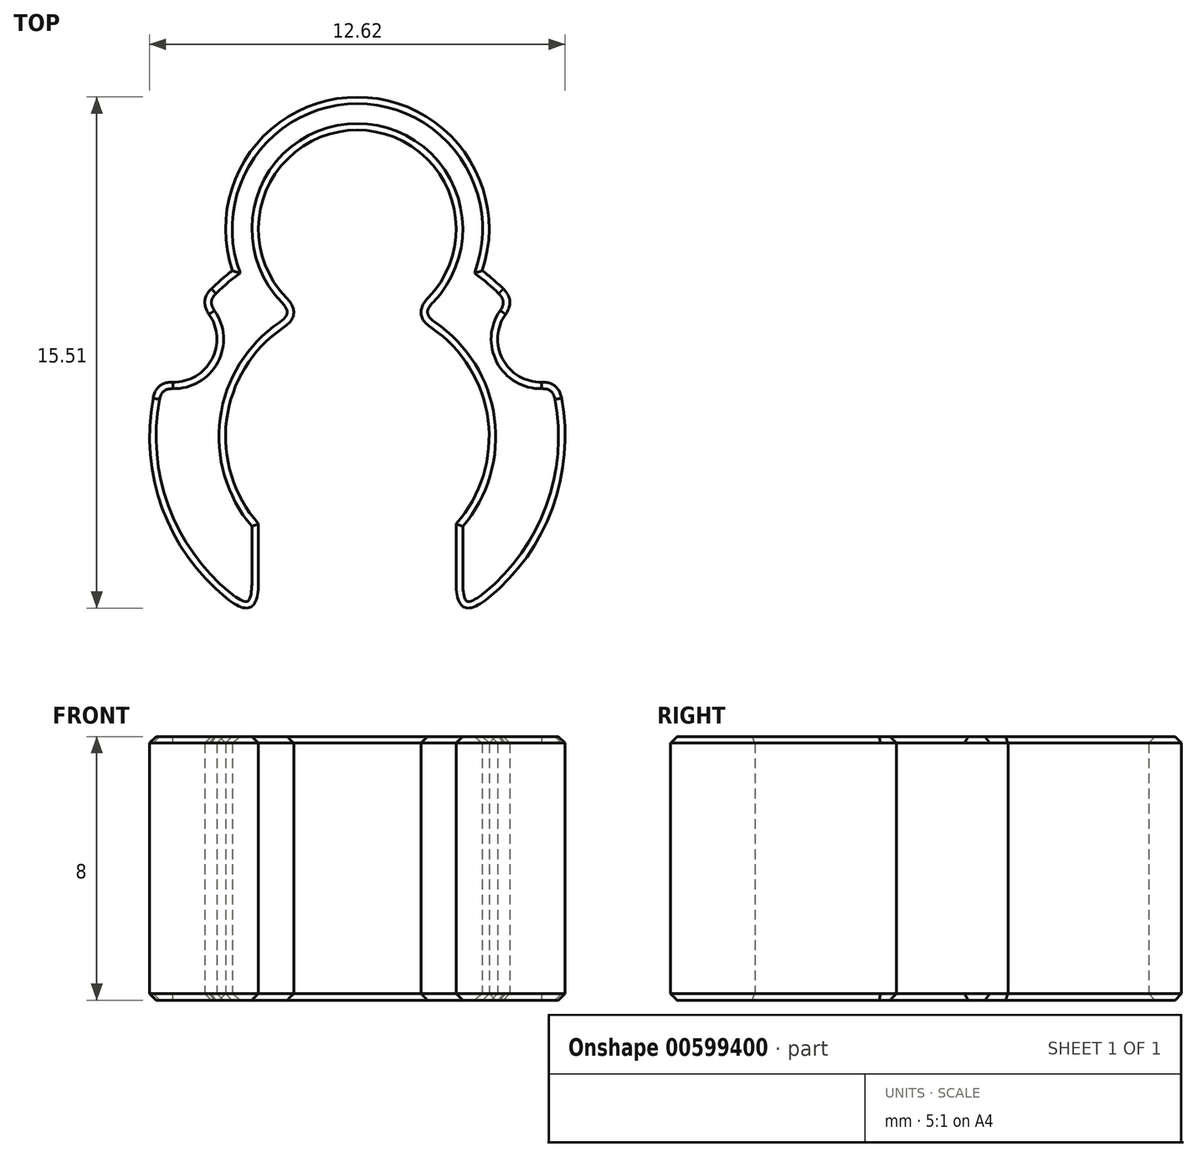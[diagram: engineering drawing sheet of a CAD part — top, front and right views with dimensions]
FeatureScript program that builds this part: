
annotation { "Feature Type Name" : "Feature", "Feature Type Description" : "" }
export const myFeature = defineFeature(function(context is Context, id is Id, definition is map)
    precondition{}
    {
        {
            var Q0;
            Q0=qCreatedBy(makeId("Top.planeOp"),FACE);
            var sketch = newSketch(context, id + "F0", { "sketchPlane" : qUnion([Q0])});
            skCircle(sketch, "E0", {"center": v(0, 0) * mm, "radius": 4 * mm});
            skCircle(sketch, "E1", {"center": v(0, 0) * mm, "radius": 6.3 * mm});
            skLineSegment(sketch, "E2.bottom", {"start": v(3, -2.65) * mm, "end": v(-3, -2.65) * mm});
            skLineSegment(sketch, "E2.top", {"start": v(3, -6.3) * mm, "end": v(-3, -6.3) * mm});
            skLineSegment(sketch, "E2.left", {"start": v(3, -2.65) * mm, "end": v(3, -6.3) * mm});
            skLineSegment(sketch, "E2.right", {"start": v(-3, -2.65) * mm, "end": v(-3, -6.3) * mm});
            skPoint(sketch, "E2.middle", {"position": v(0, -4.48) * mm});
            skCircle(sketch, "E3", {"center": v(0, 6.3) * mm, "radius": 3 * mm});
            skCircle(sketch, "E4", {"center": v(0, 6.3) * mm, "radius": 4 * mm});
            skCircle(sketch, "E5", {"center": v(-5.57, 2.96) * mm, "radius": 1.3 * mm});
            skLineSegment(sketch, "E6", {"start": v(0, 0) * mm, "end": v(-5.57, 2.96) * mm, "construction": true});
            skLineSegment(sketch, "E7", {"start": v(0, 0) * mm, "end": v(-3.8, 5.04) * mm, "construction": true});
            skLineSegment(sketch, "E8", {"start": v(0, 0) * mm, "end": v(3.8, 5.04) * mm, "construction": true});
            skLineSegment(sketch, "E9", {"start": v(0, 0) * mm, "end": v(5.57, 2.96) * mm, "construction": true});
            skCircle(sketch, "E10", {"center": v(5.57, 2.96) * mm, "radius": 1.3 * mm});
            skPoint(sketch, "E11", {"position": v(-1.5, 3.7) * mm});
            skPoint(sketch, "E12", {"position": v(1.5, 3.7) * mm});
            skSolve(sketch);
        }
        {
            var Q0;
            {var subQ3=sQuery(id+"F0.wireOp",EDGE,"E1");var subQ5=sQuery(id+"F0.wireOp",EDGE,"E4");var subQ6=makeQuery(id+"F0.imprint","INTERSECT",VERTEX,{"disambiguationData":[OD(1.0)],"derivedFrom":[subQ3,subQ5]});Q0=makeQuery(id+"F0.imprint","IMPRINT",FACE,{"disambiguationData":[TD([[makeQuery(id+"F0.imprint","IMPRINT",EDGE,{"disambiguationData":[TD([[subQ6,-1.0]])],"derivedFrom":subQ3}),1.0]])]});}
            var Q1;
            {var subQ0=sQuery(id+"F0.wireOp",EDGE,"E10");var subQ1=sQuery(id+"F0.wireOp",EDGE,"E1");var subQ9=makeQuery(id+"F0.imprint","INTERSECT",VERTEX,{"disambiguationData":[OD(0.0)],"derivedFrom":[subQ1,subQ0]});Q1=makeQuery(id+"F0.imprint","IMPRINT",FACE,{"disambiguationData":[TD([[makeQuery(id+"F0.imprint","IMPRINT",EDGE,{"disambiguationData":[TD([[subQ9,-1.0]])],"derivedFrom":subQ1}),1.0]])]});}
            var Q2;
            {var subQ0=sQuery(id+"F0.wireOp",EDGE,"E3");var subQ1=sQuery(id+"F0.wireOp",EDGE,"E0");var subQ2=makeQuery(id+"F0.imprint","INTERSECT",VERTEX,{"disambiguationData":[OD(0.0)],"derivedFrom":[subQ1,subQ0]});Q2=makeQuery(id+"F0.imprint","IMPRINT",FACE,{"disambiguationData":[TD([[makeQuery(id+"F0.imprint","IMPRINT",EDGE,{"disambiguationData":[TD([[subQ2,1.0]])],"derivedFrom":subQ1}),-1.0]])]});}
            var Q3;
            {var subQ0=sQuery(id+"F0.wireOp",EDGE,"E4");var subQ1=sQuery(id+"F0.wireOp",EDGE,"E1");var subQ2=makeQuery(id+"F0.imprint","INTERSECT",VERTEX,{"disambiguationData":[OD(0.0)],"derivedFrom":[subQ1,subQ0]});Q3=makeQuery(id+"F0.imprint","IMPRINT",FACE,{"disambiguationData":[TD([[makeQuery(id+"F0.imprint","IMPRINT",EDGE,{"disambiguationData":[TD([[subQ2,-1.0]])],"derivedFrom":subQ1}),-1.0]])]});}
            var Q4;
            {var subQ0=sQuery(id+"F0.wireOp",EDGE,"E3");var subQ1=sQuery(id+"F0.wireOp",EDGE,"E0");var subQ2=makeQuery(id+"F0.imprint","INTERSECT",VERTEX,{"disambiguationData":[OD(1.0)],"derivedFrom":[subQ1,subQ0]});Q4=makeQuery(id+"F0.imprint","IMPRINT",FACE,{"disambiguationData":[TD([[makeQuery(id+"F0.imprint","IMPRINT",EDGE,{"disambiguationData":[TD([[subQ2,-1.0]])],"derivedFrom":subQ1}),-1.0]])]});}
            extrude(context, id + "F1", {"entities" : qUnion([Q0, Q1, Q2, Q3, Q4]), "depth" : 8 * mm, "offsetDistance" : 25 * mm});
        }
        {
            var Q0;
            {var subQ0=sQuery(id+"F0.wireOp",EDGE,"E5");var subQ1=sQuery(id+"F0.wireOp",EDGE,"E1");Q0=makeQuery(id+"F1.opExtrude","SWEPT_EDGE",EDGE,{"disambiguationData":[OSD([subQ1,subQ0]),TDD([makeQuery(id+"F0.imprint","INTERSECT",VERTEX,{"disambiguationData":[OD(0.0)],"derivedFrom":[subQ1,subQ0]})])]});}
            var Q1;
            {var subQ0=sQuery(id+"F0.wireOp",EDGE,"E5");var subQ1=sQuery(id+"F0.wireOp",EDGE,"E1");Q1=makeQuery(id+"F1.opExtrude","SWEPT_EDGE",EDGE,{"disambiguationData":[OSD([subQ1,subQ0]),TDD([makeQuery(id+"F0.imprint","INTERSECT",VERTEX,{"disambiguationData":[OD(1.0)],"derivedFrom":[subQ1,subQ0]})])]});}
            var Q2;
            {var subQ0=sQuery(id+"F0.wireOp",EDGE,"E3");var subQ1=sQuery(id+"F0.wireOp",EDGE,"E0");Q2=makeQuery(id+"F1.opExtrude","SWEPT_EDGE",EDGE,{"disambiguationData":[OSD([subQ1,subQ0]),TDD([makeQuery(id+"F0.imprint","INTERSECT",VERTEX,{"disambiguationData":[OD(1.0)],"derivedFrom":[subQ1,subQ0]})])]});}
            var Q3;
            {var subQ0=sQuery(id+"F0.wireOp",EDGE,"E10");var subQ1=sQuery(id+"F0.wireOp",EDGE,"E1");Q3=makeQuery(id+"F1.opExtrude","SWEPT_EDGE",EDGE,{"disambiguationData":[OSD([subQ1,subQ0]),TDD([makeQuery(id+"F0.imprint","INTERSECT",VERTEX,{"disambiguationData":[OD(0.0)],"derivedFrom":[subQ1,subQ0]})])]});}
            var Q4;
            {var subQ0=sQuery(id+"F0.wireOp",EDGE,"E3");var subQ1=sQuery(id+"F0.wireOp",EDGE,"E0");Q4=makeQuery(id+"F1.opExtrude","SWEPT_EDGE",EDGE,{"disambiguationData":[OSD([subQ1,subQ0]),TDD([makeQuery(id+"F0.imprint","INTERSECT",VERTEX,{"disambiguationData":[OD(0.0)],"derivedFrom":[subQ1,subQ0]})])]});}
            var Q5;
            {var subQ0=sQuery(id+"F0.wireOp",EDGE,"E10");var subQ1=sQuery(id+"F0.wireOp",EDGE,"E1");Q5=makeQuery(id+"F1.opExtrude","SWEPT_EDGE",EDGE,{"disambiguationData":[OSD([subQ1,subQ0]),TDD([makeQuery(id+"F0.imprint","INTERSECT",VERTEX,{"disambiguationData":[OD(1.0)],"derivedFrom":[subQ1,subQ0]})])]});}
            var Q6;
            Q6=makeQuery(id+"F1.opExtrude","SWEPT_EDGE",EDGE,{"disambiguationData":[OSD([sQuery(id+"F0.wireOp",EDGE,"E1"),sQuery(id+"F0.wireOp",EDGE,"E2.right")])]});
            var Q7;
            Q7=makeQuery(id+"F1.opExtrude","SWEPT_EDGE",EDGE,{"disambiguationData":[OSD([sQuery(id+"F0.wireOp",EDGE,"E1"),sQuery(id+"F0.wireOp",EDGE,"E2.left")])]});
            fillet(context, id + "F2", {"entities" : qUnion([Q0, Q1, Q2, Q3, Q4, Q5, Q6, Q7]), "radius" : 0.6 * mm, "tangentPropagation" : true, "rho" : 0.5, "crossSection" : FilletCrossSection.CONIC, "allowEdgeOverflow" : false});
        }
        {
            var Q0;
            Q0=makeQuery(id+"F1.opExtrude","CAP_FACE",FACE,{"disambiguationData":[OSD([sQuery(id+"F0.wireOp",EDGE,"E0"),sQuery(id+"F0.wireOp",EDGE,"E1"),sQuery(id+"F0.wireOp",EDGE,"E2.left"),sQuery(id+"F0.wireOp",EDGE,"E2.right"),sQuery(id+"F0.wireOp",EDGE,"E3"),sQuery(id+"F0.wireOp",EDGE,"E4"),sQuery(id+"F0.wireOp",EDGE,"E5"),sQuery(id+"F0.wireOp",EDGE,"E10")])],"isStart":false});
            var Q1;
            Q1=makeQuery(id+"F1.opExtrude","CAP_FACE",FACE,{"disambiguationData":[OSD([sQuery(id+"F0.wireOp",EDGE,"E0"),sQuery(id+"F0.wireOp",EDGE,"E1"),sQuery(id+"F0.wireOp",EDGE,"E2.left"),sQuery(id+"F0.wireOp",EDGE,"E2.right"),sQuery(id+"F0.wireOp",EDGE,"E3"),sQuery(id+"F0.wireOp",EDGE,"E4"),sQuery(id+"F0.wireOp",EDGE,"E5"),sQuery(id+"F0.wireOp",EDGE,"E10")])],"isStart":true});
            chamfer(context, id + "F3", {"entities" : qUnion([Q0, Q1]), "width" : 0.2 * mm, "tangentPropagation" : true});
        }
    });
